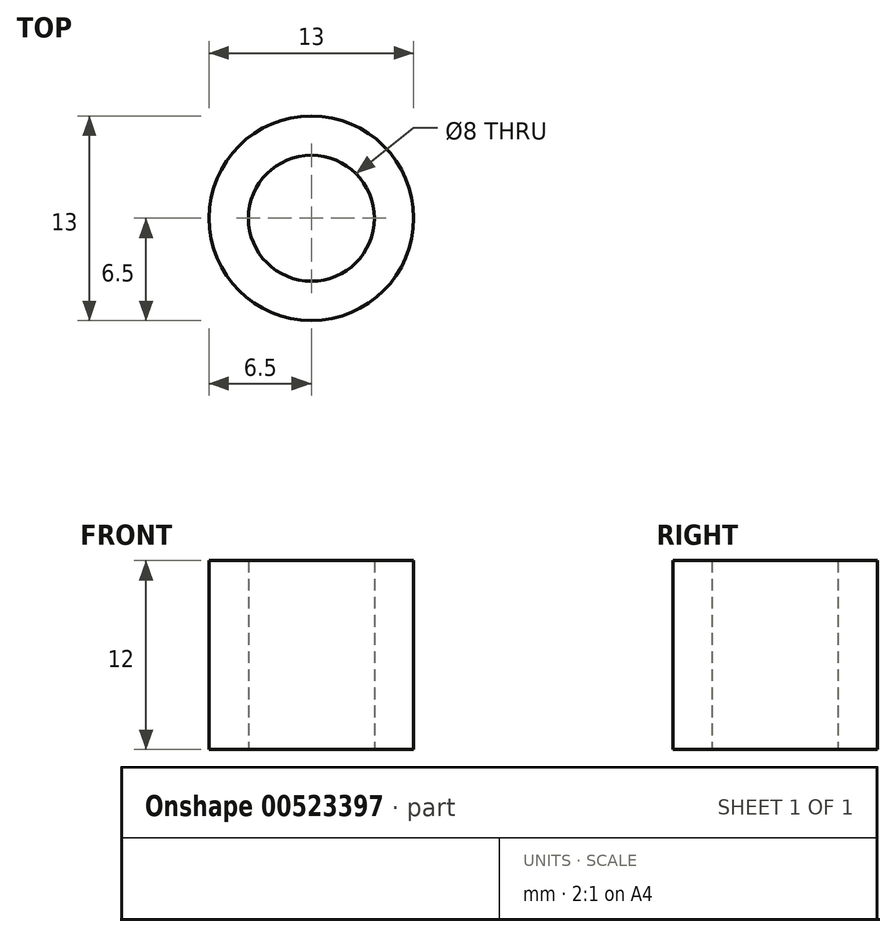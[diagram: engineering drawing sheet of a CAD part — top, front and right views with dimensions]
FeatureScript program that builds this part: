
annotation { "Feature Type Name" : "Feature", "Feature Type Description" : "" }
export const myFeature = defineFeature(function(context is Context, id is Id, definition is map)
    precondition{}
    {
        {
            var Q0;
            Q0=qCreatedBy(makeId("Top.planeOp"),FACE);
            var sketch = newSketch(context, id + "F0", { "sketchPlane" : qUnion([Q0])});
            skCircle(sketch, "E0", {"center": v(0, 0) * mm, "radius": 4 * mm});
            skCircle(sketch, "E1", {"center": v(0, 0) * mm, "radius": 6.5 * mm});
            skSolve(sketch);
        }
        {
            var Q0;
            Q0 = qSketchRegion(id + "F0", true);
            extrude(context, id + "F1", {"entities" : qUnion([Q0]), "depth" : 12 * mm, "offsetDistance" : 25 * mm});
        }
    });
